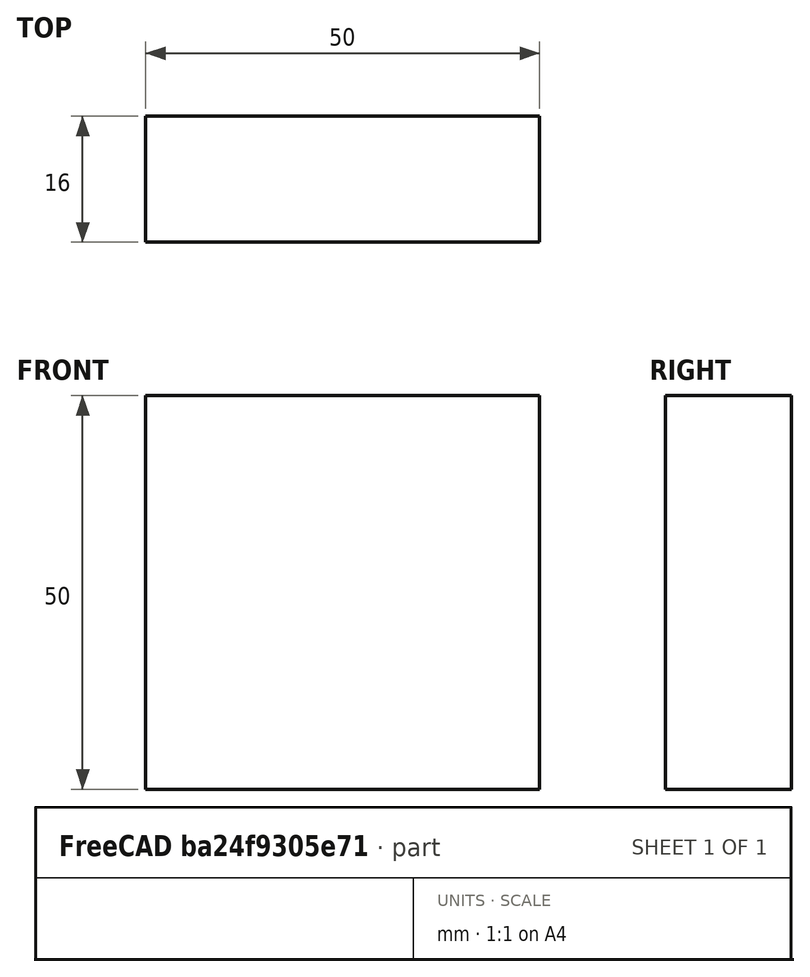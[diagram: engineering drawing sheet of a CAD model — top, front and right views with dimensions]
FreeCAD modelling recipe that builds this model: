
FCSTD DOCUMENT  (FreeCAD 0.15R4671 (Git))
Label: Flat Bar 50x16 EN10058 S235JR
License: All rights reserved
LicenseURL: http://en.wikipedia.org/wiki/All_rights_reserved
objects: Sketcher::SketchObject×1, Part::Extrusion×1
note: 2 computed .brp shape members not serialized (recipe doc carries the construction recipe); baked Part::Feature solids carry a one-line shape summary decoded from their .brp

FEATURE [Sketcher::SketchObject] Sketch
  sketch-geometry (4):
    g0: LineSegment StartX=-25 StartY=-8 StartZ=0 EndX=25 EndY=-8 EndZ=0
    g1: LineSegment StartX=25 StartY=-8 StartZ=0 EndX=25 EndY=8 EndZ=0
    g2: LineSegment StartX=25 StartY=8 StartZ=0 EndX=-25 EndY=8 EndZ=0
    g3: LineSegment StartX=-25 StartY=8 StartZ=0 EndX=-25 EndY=-8 EndZ=0
  constraints (12):
    c: Coincident(g0,g1)
    c: Coincident(g1,g2)
    c: Coincident(g2,g3)
    c: Coincident(g3,g0)
    c: Horizontal(g0)
    c: Horizontal(g2)
    c: Vertical(g1)
    c: Vertical(g3)
    c: Symmetric(g1,g2,g-2)
    c: Symmetric(g0,g1,g-1)
    c: DistanceY(g1) = 16
    c: DistanceX(g0) = 50
FEATURE [Part::Extrusion] Extrude  label="Flat Bar 50x16 EN10058 S235JR"
  Base = -> Sketch
  Dir = (0,0,50)
  Solid = true
